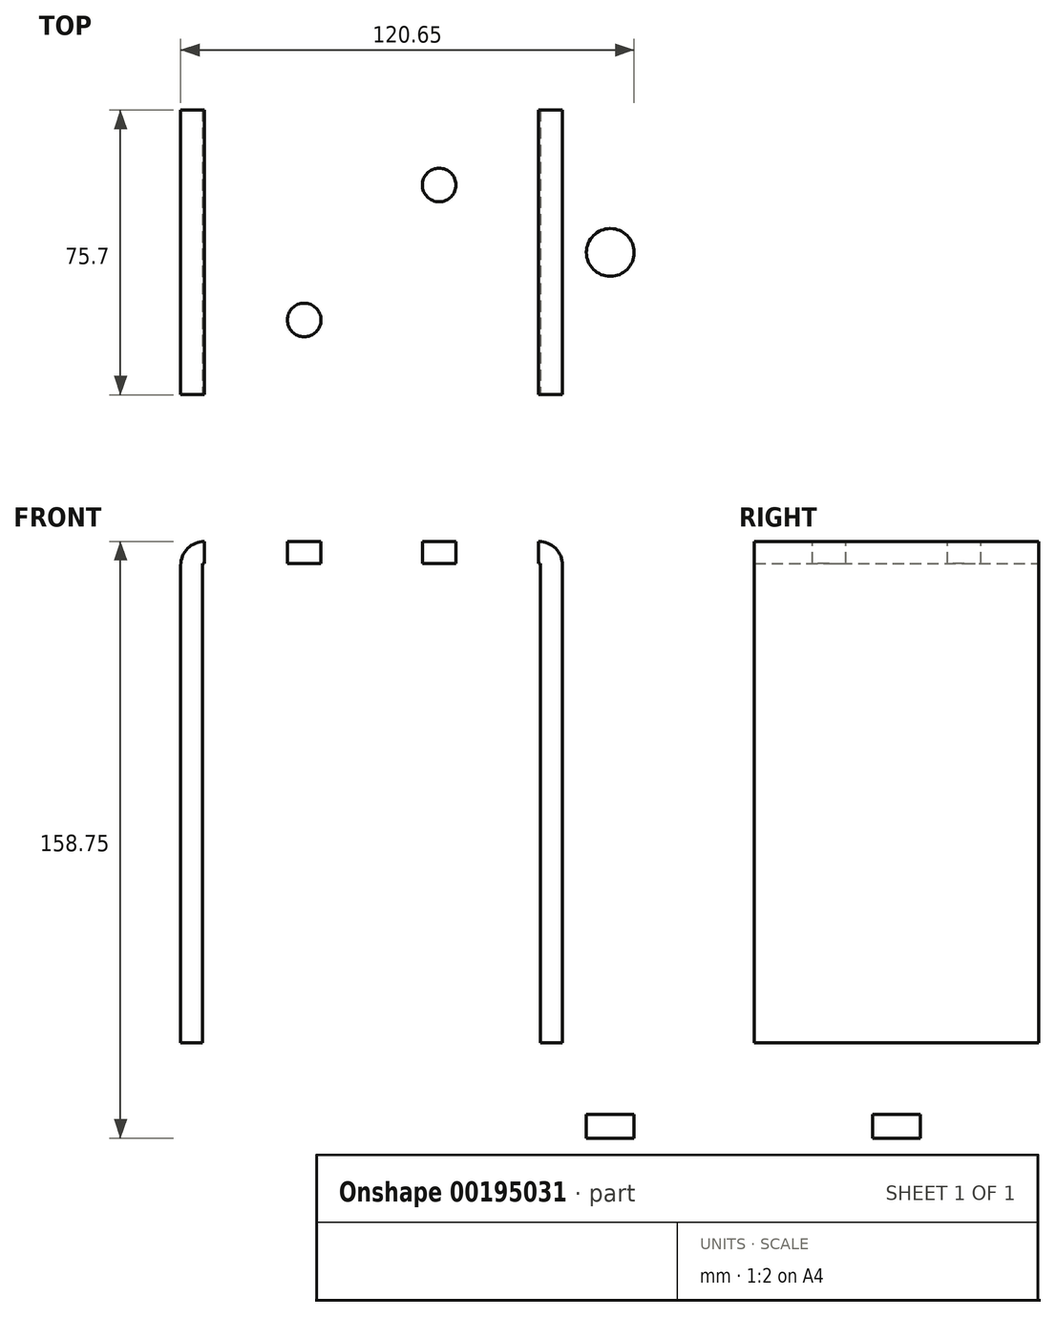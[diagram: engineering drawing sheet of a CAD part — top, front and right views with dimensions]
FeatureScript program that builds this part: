
annotation { "Feature Type Name" : "Feature", "Feature Type Description" : "" }
export const myFeature = defineFeature(function(context is Context, id is Id, definition is map)
    precondition{}
    {
        {
            var Q0;
            Q0=qCreatedBy(makeId("Front.planeOp"),FACE);
            var sketch = newSketch(context, id + "F0", { "sketchPlane" : qUnion([Q0])});
            skLineSegment(sketch, "E0.bottom", {"start": v(-44.45, 76.2) * mm, "end": v(44.45, 76.2) * mm});
            skLineSegment(sketch, "E0.top", {"start": v(-44.45, -76.2) * mm, "end": v(44.45, -76.2) * mm});
            skLineSegment(sketch, "E0.left", {"start": v(-50.8, 69.85) * mm, "end": v(-50.8, -69.85) * mm});
            skLineSegment(sketch, "E0.right", {"start": v(50.8, 69.85) * mm, "end": v(50.8, -69.85) * mm});
            skPoint(sketch, "E0.middle", {"position": v(0, 0) * mm});
            skPoint(sketch, "E1.visualSharp", {"position": v(-50.8, 76.2) * mm});
            skArc(sketch, "E1.filletArc", {"start": v(-44.45, 76.2) * mm, "mid": v(-48.94, 74.34) * mm, "end": v(-50.8, 69.85) * mm});
            skPoint(sketch, "E2.visualSharp", {"position": v(50.8, 76.2) * mm});
            skArc(sketch, "E2.filletArc", {"start": v(50.8, 69.85) * mm, "mid": v(48.94, 74.34) * mm, "end": v(44.45, 76.2) * mm});
            skPoint(sketch, "E3.visualSharp", {"position": v(50.8, -76.2) * mm});
            skArc(sketch, "E3.filletArc", {"start": v(44.45, -76.2) * mm, "mid": v(48.94, -74.34) * mm, "end": v(50.8, -69.85) * mm});
            skPoint(sketch, "E4.visualSharp", {"position": v(-50.8, -76.2) * mm});
            skArc(sketch, "E4.filletArc", {"start": v(-50.8, -69.85) * mm, "mid": v(-48.94, -74.34) * mm, "end": v(-44.45, -76.2) * mm});
            skLineSegment(sketch, "E5.0", {"start": v(-44.96, 70.36) * mm, "end": v(44.96, 70.36) * mm});
            skLineSegment(sketch, "E5.1", {"start": v(-44.96, 70.36) * mm, "end": v(-44.96, -70.36) * mm});
            skLineSegment(sketch, "E5.2", {"start": v(-44.96, -70.36) * mm, "end": v(44.96, -70.36) * mm});
            skLineSegment(sketch, "E5.3", {"start": v(44.96, 70.36) * mm, "end": v(44.96, -70.36) * mm});
            skSolve(sketch);
        }
        {
            var Q0;
            Q0=makeQuery(id+"F0.imprint","IMPRINT",FACE,{"disambiguationData":[TD([[makeQuery(id+"F0.imprint","IMPRINT",EDGE,{"derivedFrom":sQuery(id+"F0.wireOp",EDGE,"E0.bottom")}),-1.0]])]});
            extrude(context, id + "F1", {"entities" : qUnion([Q0]), "endBound" : BoundingType.SYMMETRIC, "oppositeDirection" : true, "depth" : 75.7 * mm});
        }
        {
            var Q0;
            Q0=makeQuery(id+"F1.opExtrude","SWEPT_FACE",FACE,{"disambiguationData":[OSD([sQuery(id+"F0.wireOp",EDGE,"E0.bottom")])]});
            var sketch = newSketch(context, id + "F2", { "sketchPlane" : qUnion([Q0])});
            skCircle(sketch, "E6", {"center": v(-17.96, 17.96) * mm, "radius": 4.47 * mm});
            skCircle(sketch, "E7.MirrorC", {"center": v(17.96, 17.96) * mm, "radius": 4.47 * mm});
            skCircle(sketch, "E8.MirrorC", {"center": v(17.96, -17.96) * mm, "radius": 4.47 * mm});
            skCircle(sketch, "E9.MirrorC", {"center": v(-17.96, -17.96) * mm, "radius": 4.47 * mm});
            skCircle(sketch, "E10", {"center": v(0, 0) * mm, "radius": 12.7 * mm});
            skSolve(sketch);
        }
        {
            var Q0;
            Q0=makeQuery(id+"F2.imprint","IMPRINT",FACE,{"disambiguationData":[TD([[makeQuery(id+"F2.imprint","IMPRINT",EDGE,{"derivedFrom":sQuery(id+"F2.wireOp",EDGE,"E6")}),1.0]])]});
            var Q1;
            Q1=makeQuery(id+"F2.imprint","IMPRINT",FACE,{"disambiguationData":[TD([[makeQuery(id+"F2.imprint","IMPRINT",EDGE,{"derivedFrom":sQuery(id+"F2.wireOp",EDGE,"E7.MirrorC")}),-1.0]])]});
            var Q2;
            Q2=makeQuery(id+"F2.imprint","IMPRINT",FACE,{"disambiguationData":[TD([[makeQuery(id+"F2.imprint","IMPRINT",EDGE,{"derivedFrom":sQuery(id+"F2.wireOp",EDGE,"E8.MirrorC")}),1.0]])]});
            var Q3;
            Q3=makeQuery(id+"F2.imprint","IMPRINT",FACE,{"disambiguationData":[TD([[makeQuery(id+"F2.imprint","IMPRINT",EDGE,{"derivedFrom":sQuery(id+"F2.wireOp",EDGE,"E9.MirrorC")}),-1.0]])]});
            var Q4;
            Q4=makeQuery(id+"F2.imprint","IMPRINT",FACE,{"disambiguationData":[TD([[makeQuery(id+"F2.imprint","IMPRINT",EDGE,{"derivedFrom":sQuery(id+"F2.wireOp",EDGE,"E10")}),1.0]])]});
            extrude(context, id + "F3", {"entities" : qUnion([Q0, Q1, Q2, Q3, Q4]), "operationType" : NewBodyOperationType.REMOVE, "oppositeDirection" : true, "depth" : 25.4 * mm});
        }
        {
            var Q0;
            Q0=makeQuery(id+"F1.opExtrude","SWEPT_FACE",FACE,{"disambiguationData":[OSD([sQuery(id+"F0.wireOp",EDGE,"E0.top")])]});
            var sketch = newSketch(context, id + "F4", { "sketchPlane" : qUnion([Q0])});
            skLineSegment(sketch, "E11.bottom", {"start": v(-92.08, 38.1) * mm, "end": v(92.08, 38.1) * mm});
            skLineSegment(sketch, "E11.top", {"start": v(-92.08, -38.1) * mm, "end": v(92.08, -38.1) * mm});
            skLineSegment(sketch, "E11.left", {"start": v(-92.07, 38.1) * mm, "end": v(-92.08, -38.1) * mm});
            skLineSegment(sketch, "E11.right", {"start": v(92.08, 38.1) * mm, "end": v(92.08, -38.1) * mm});
            skPoint(sketch, "E11.middle", {"position": v(0, 0) * mm});
            skSolve(sketch);
        }
        {
            var Q0;
            Q0=makeQuery(id+"F4.imprint","IMPRINT",FACE,{"disambiguationData":[TD([[makeQuery(id+"F4.imprint","IMPRINT",EDGE,{"derivedFrom":sQuery(id+"F4.wireOp",EDGE,"E11.bottom")}),-1.0]])]});
            var Q1;
            {var subQ0=sQuery(id+"F0.wireOp",EDGE,"E0.top");Q1=makeQuery(id+"F4.imprint","IMPRINT",FACE,{"disambiguationData":[TD([[makeQuery(id+"F4.imprint","IMPRINT",EDGE,{"derivedFrom":makeQuery(id+"F1.opExtrude","CAP_EDGE",EDGE,{"disambiguationData":[OSD([subQ0])],"isStart":true})}),-1.0]])]});}
            extrude(context, id + "F5", {"entities" : qUnion([Q0, Q1]), "operationType" : NewBodyOperationType.ADD, "depth" : 6.35 * mm});
        }
        {
            var Q0;
            Q0=makeQuery(id+"F5.opExtrude","CAP_FACE",FACE,{"disambiguationData":[OSD([sQuery(id+"F4.wireOp",EDGE,"E11.bottom"),sQuery(id+"F4.wireOp",EDGE,"E11.top"),sQuery(id+"F4.wireOp",EDGE,"E11.left"),sQuery(id+"F4.wireOp",EDGE,"E11.right")])],"isStart":false});
            var sketch = newSketch(context, id + "F6", { "sketchPlane" : qUnion([Q0])});
            skCircle(sketch, "E12", {"center": v(-63.5, 0) * mm, "radius": 6.35 * mm});
            skCircle(sketch, "E13", {"center": v(0, 0) * mm, "radius": 8.9 * mm});
            skCircle(sketch, "E14.MirrorC", {"center": v(63.5, 0) * mm, "radius": 6.35 * mm});
            skSolve(sketch);
        }
        {
            var Q0;
            Q0=makeQuery(id+"F6.imprint","IMPRINT",FACE,{"disambiguationData":[TD([[makeQuery(id+"F6.imprint","IMPRINT",EDGE,{"derivedFrom":sQuery(id+"F6.wireOp",EDGE,"E14.MirrorC")}),-1.0]])]});
            var Q1;
            Q1=makeQuery(id+"F6.imprint","IMPRINT",FACE,{"disambiguationData":[TD([[makeQuery(id+"F6.imprint","IMPRINT",EDGE,{"derivedFrom":sQuery(id+"F6.wireOp",EDGE,"E13")}),1.0]])]});
            var Q2;
            Q2=makeQuery(id+"F6.imprint","IMPRINT",FACE,{"disambiguationData":[TD([[makeQuery(id+"F6.imprint","IMPRINT",EDGE,{"derivedFrom":sQuery(id+"F6.wireOp",EDGE,"E12")}),1.0]])]});
            extrude(context, id + "F7", {"entities" : qUnion([Q0, Q1, Q2]), "operationType" : NewBodyOperationType.REMOVE, "oppositeDirection" : true, "depth" : 25.4 * mm});
        }
    });
